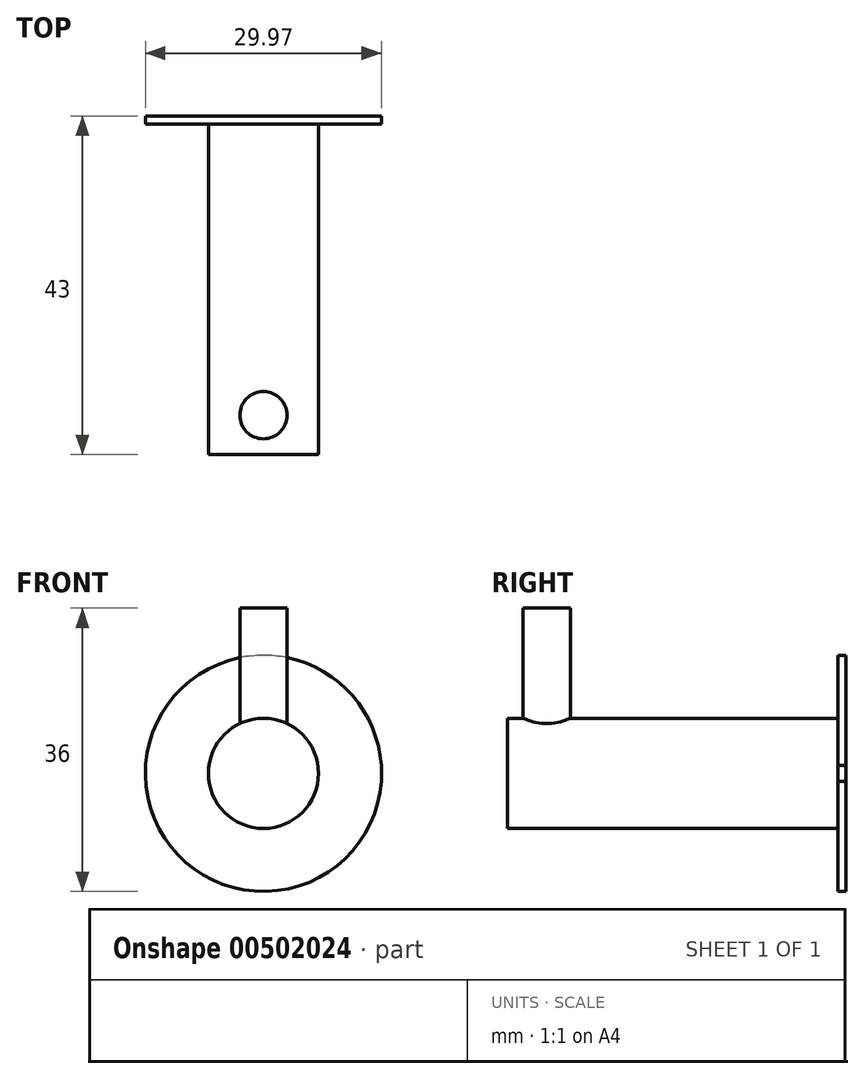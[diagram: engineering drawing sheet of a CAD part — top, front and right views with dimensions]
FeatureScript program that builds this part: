
annotation { "Feature Type Name" : "Feature", "Feature Type Description" : "" }
export const myFeature = defineFeature(function(context is Context, id is Id, definition is map)
    precondition{}
    {
        {
            var Q0;
            Q0=qCreatedBy(makeId("Front.planeOp"),FACE);
            var sketch = newSketch(context, id + "F0", { "sketchPlane" : qUnion([Q0])});
            skCircle(sketch, "E0", {"center": v(0, 0) * mm, "radius": 15 * mm});
            skSolve(sketch);
        }
        {
            var Q0;
            Q0 = qSketchRegion(id + "F0", true);
            extrude(context, id + "F1", {"entities" : qUnion([Q0]), "depth" : 1 * mm, "offsetDistance" : 25 * mm});
        }
        {
            var Q0;
            Q0=makeQuery(id+"F1.opExtrude","CAP_FACE",FACE,{"disambiguationData":[OSD([sQuery(id+"F0.wireOp",EDGE,"E0")])],"isStart":false});
            var sketch = newSketch(context, id + "F2", { "sketchPlane" : qUnion([Q0])});
            skCircle(sketch, "E1", {"center": v(0, 0) * mm, "radius": 7 * mm});
            skSolve(sketch);
        }
        {
            var Q0;
            Q0 = qSketchRegion(id + "F2", true);
            extrude(context, id + "F3", {"entities" : qUnion([Q0]), "operationType" : NewBodyOperationType.ADD, "depth" : 42 * mm, "offsetDistance" : 25 * mm});
        }
        {
            var Q0;
            Q0=qCreatedBy(makeId("Top.planeOp"),FACE);
            var sketch = newSketch(context, id + "F4", { "sketchPlane" : qUnion([Q0])});
            skCircle(sketch, "E2", {"center": v(0, -38) * mm, "radius": 3 * mm});
            skSolve(sketch);
        }
        {
            var Q0;
            Q0 = qSketchRegion(id + "F4", true);
            extrude(context, id + "F5", {"entities" : qUnion([Q0]), "operationType" : NewBodyOperationType.ADD, "depth" : 21 * mm, "offsetDistance" : 25 * mm});
        }
        {
            var Q0;
            Q0=makeQuery(id+"F1.opExtrude","CAP_FACE",FACE,{"disambiguationData":[OSD([sQuery(id+"F0.wireOp",EDGE,"E0")])],"isStart":false});
            var sketch = newSketch(context, id + "F6", { "sketchPlane" : qUnion([Q0])});
            skLineSegment(sketch, "E3", {"start": v(14.97, 1) * mm, "end": v(14.97, -1) * mm});
            skLineSegment(sketch, "E4", {"start": v(14.97, -1) * mm, "end": v(16.97, -1) * mm});
            skLineSegment(sketch, "E5", {"start": v(16.97, -1) * mm, "end": v(16.97, 1) * mm});
            skLineSegment(sketch, "E6", {"start": v(16.97, 1) * mm, "end": v(14.97, 1) * mm});
            skSolve(sketch);
        }
        {
            var Q0;
            Q0 = qSketchRegion(id + "F6", true);
            extrude(context, id + "F7", {"entities" : qUnion([Q0]), "operationType" : NewBodyOperationType.REMOVE, "endBound" : BoundingType.THROUGH_ALL, "oppositeDirection" : true, "depth" : 25 * mm, "offsetDistance" : 25 * mm});
        }
    });
